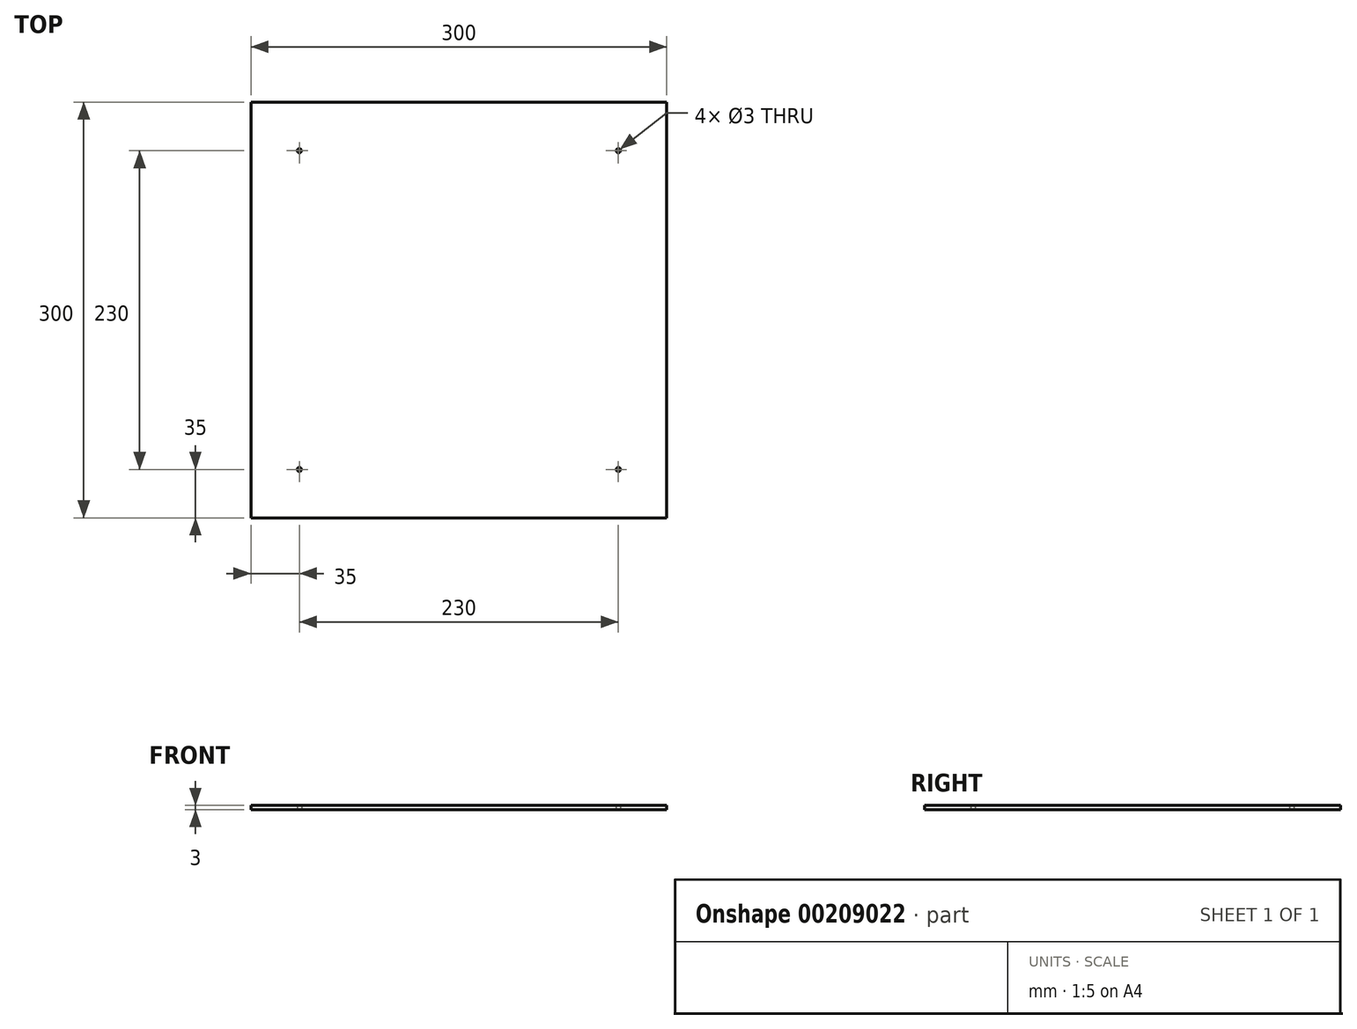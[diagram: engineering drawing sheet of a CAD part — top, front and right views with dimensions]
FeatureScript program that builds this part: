
annotation { "Feature Type Name" : "Feature", "Feature Type Description" : "" }
export const myFeature = defineFeature(function(context is Context, id is Id, definition is map)
    precondition{}
    {
        {
            var Q0;
            Q0=qCreatedBy(makeId("Top.planeOp"),FACE);
            var sketch = newSketch(context, id + "F0", { "sketchPlane" : qUnion([Q0])});
            skLineSegment(sketch, "E0.bottom", {"start": v(150, -150) * mm, "end": v(-150, -150) * mm});
            skLineSegment(sketch, "E0.top", {"start": v(150, 150) * mm, "end": v(-150, 150) * mm});
            skLineSegment(sketch, "E0.left", {"start": v(150, -150) * mm, "end": v(150, 150) * mm});
            skLineSegment(sketch, "E0.right", {"start": v(-150, -150) * mm, "end": v(-150, 150) * mm});
            skPoint(sketch, "E0.middle", {"position": v(0, 0) * mm});
            skCircle(sketch, "E1", {"center": v(115, 115) * mm, "radius": 1.5 * mm});
            skCircle(sketch, "E2.MirrorC", {"center": v(-115, 115) * mm, "radius": 1.5 * mm});
            skCircle(sketch, "E3.MirrorC", {"center": v(115, -115) * mm, "radius": 1.5 * mm});
            skCircle(sketch, "E4.MirrorC", {"center": v(-115, -115) * mm, "radius": 1.5 * mm});
            skSolve(sketch);
        }
        {
            var Q0;
            Q0=qSketchRegion(id+"F0",true);
            extrude(context, id + "F1", {"entities" : qUnion([Q0]), "depth" : 3 * mm});
        }
    });
